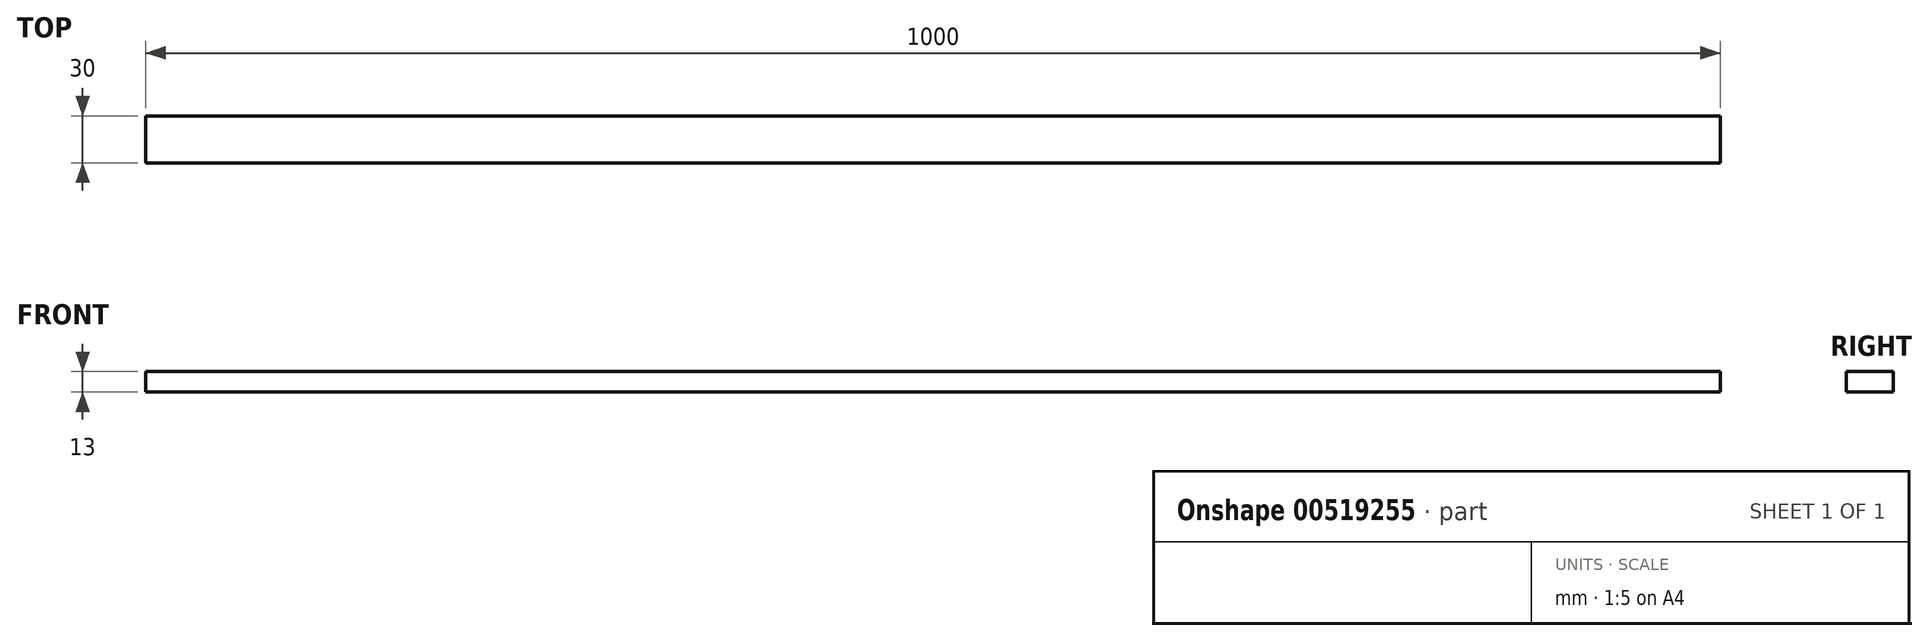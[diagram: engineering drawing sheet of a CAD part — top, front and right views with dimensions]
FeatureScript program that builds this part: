
annotation { "Feature Type Name" : "Feature", "Feature Type Description" : "" }
export const myFeature = defineFeature(function(context is Context, id is Id, definition is map)
    precondition{}
    {
        {
            var Q0;
            Q0=qCreatedBy(makeId("Right.planeOp"),FACE);
            var sketch = newSketch(context, id + "F0", { "sketchPlane" : qUnion([Q0])});
            skLineSegment(sketch, "E0.bottom", {"start": v(0, 0) * mm, "end": v(30, 0) * mm});
            skLineSegment(sketch, "E0.top", {"start": v(0, 13) * mm, "end": v(30, 13) * mm});
            skLineSegment(sketch, "E0.left", {"start": v(0, 0) * mm, "end": v(0, 13) * mm});
            skLineSegment(sketch, "E0.right", {"start": v(30, 0) * mm, "end": v(30, 13) * mm});
            skSolve(sketch);
        }
        {
            var Q0;
            Q0=qSketchRegion(id+"F0",true);
            extrude(context, id + "F1", {"entities" : qUnion([Q0]), "oppositeDirection" : true, "depth" : 1000 * mm, "offsetDistance" : 25 * mm});
        }
    });
